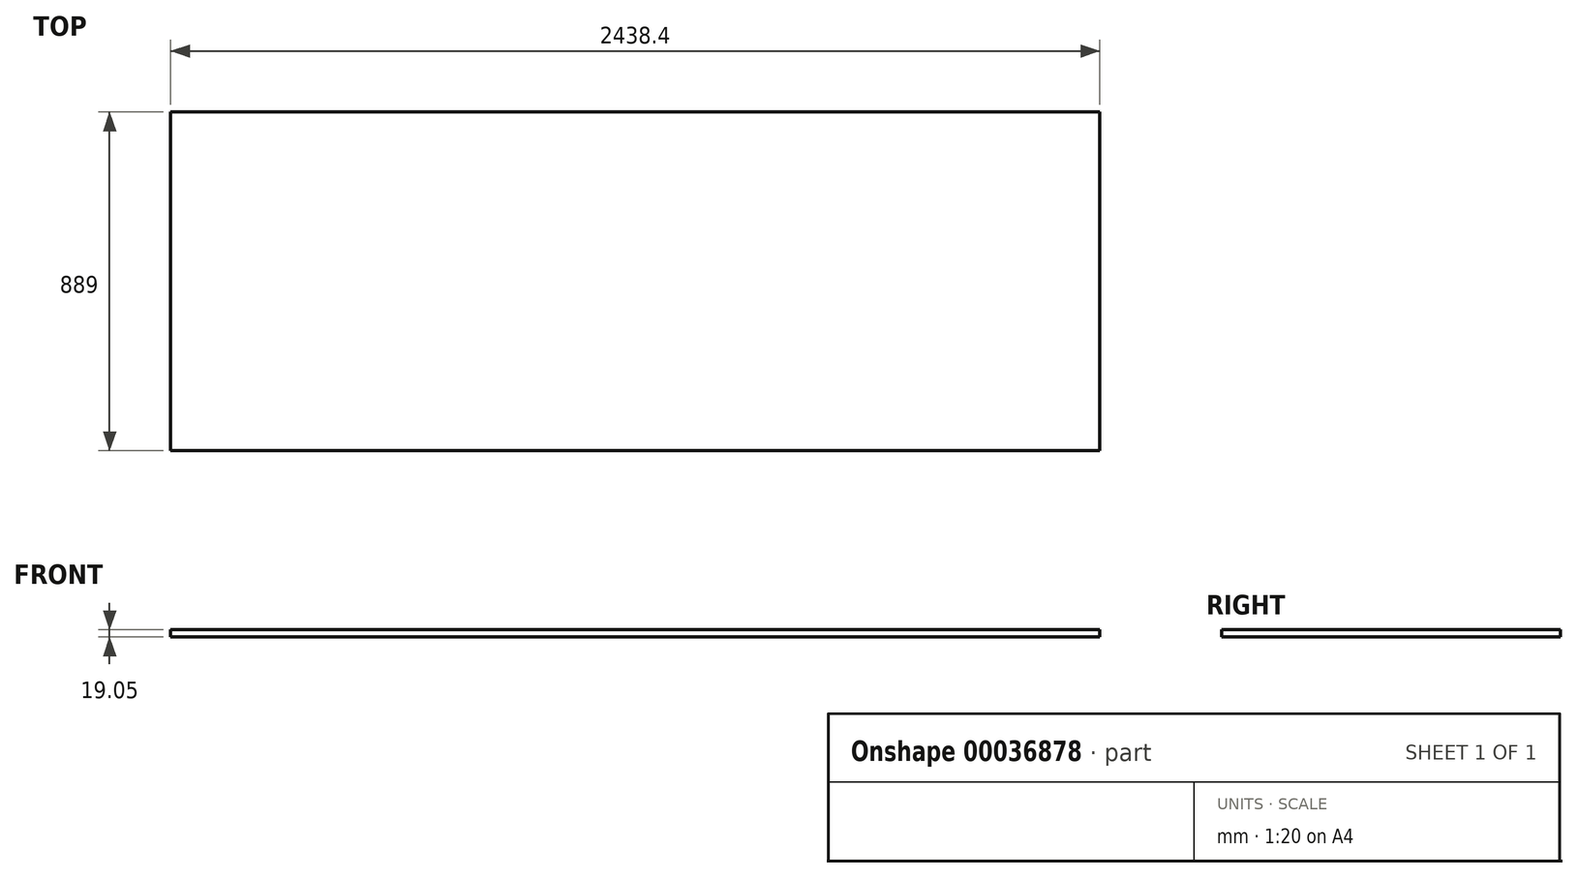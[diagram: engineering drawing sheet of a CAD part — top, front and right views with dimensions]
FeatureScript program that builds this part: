
annotation { "Feature Type Name" : "Feature", "Feature Type Description" : "" }
export const myFeature = defineFeature(function(context is Context, id is Id, definition is map)
    precondition{}
    {
        {
            var Q0;
            Q0=qCreatedBy(makeId("Top.planeOp"),FACE);
            var sketch = newSketch(context, id + "F0", { "sketchPlane" : qUnion([Q0])});
            skLineSegment(sketch, "E0.rect.bottom", {"start": v(-1219.2, 444.5) * mm, "end": v(1219.2, 444.5) * mm});
            skLineSegment(sketch, "E0.rect.top", {"start": v(-1219.2, -444.5) * mm, "end": v(1219.2, -444.5) * mm});
            skLineSegment(sketch, "E0.rect.left", {"start": v(-1219.2, 444.5) * mm, "end": v(-1219.2, -444.5) * mm});
            skLineSegment(sketch, "E0.rect.right", {"start": v(1219.2, 444.5) * mm, "end": v(1219.2, -444.5) * mm});
            skPoint(sketch, "E0.rect.middle", {"position": v(0, 0) * mm});
            skSolve(sketch);
        }
        {
            var Q0;
            Q0=makeQuery(id+"F0.imprint","IMPRINT",FACE,{"disambiguationData":[TD([[makeQuery(id+"F0.imprint","IMPRINT",EDGE,{"derivedFrom":sQuery(id+"F0.wireOp",EDGE,"E0.rect.bottom")}),-1.0]])]});
            extrude(context, id + "F1", {"entities" : qUnion([Q0]), "depth" : 19.05 * mm});
        }
    });
